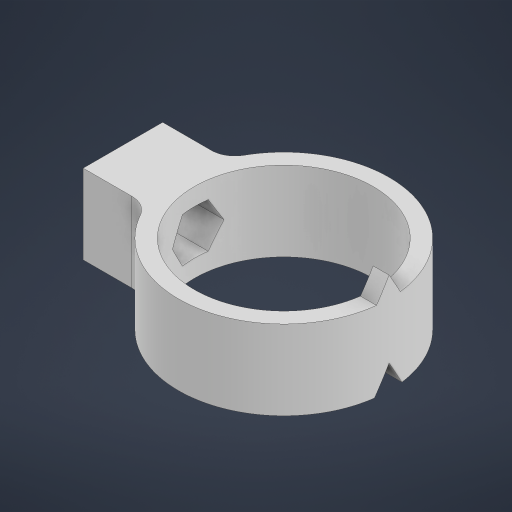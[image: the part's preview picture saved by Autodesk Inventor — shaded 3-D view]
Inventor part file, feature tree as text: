
AUTODESK INVENTOR PART (.ipt)
format: ipt  version: 2023 (Build 270158000, 158)  size: 243,712 bytes
history: native  units: mm
features: extrude x6, sketch x5, plane x2, fillet x1, projected_geometry x1
ambient origin geometry x8: Origin, YZ Plane, XZ Plane, XY Plane, X Axis, Y Axis, Z Axis, Center Point
bodies: Solid1 (feature_tree)
feature tree (15):
  extrude  "Extrusion1"  Depth=2.0mm
  plane  "Work Plane1"
  extrude  "Extrusion2"  Depth=10.0mm
  extrude  "Extrusion3"  TaperAngle=60.0deg  [1 undecoded]
  plane  "Work Plane2"
  extrude  "Extrusion4"  Depth=3.0mm TaperAngle=0.0deg
  sketch  "Sketch7"  dims[d11=60.0deg d12=12.25mm d13=0.0mm d14=-20.25mm d16=0.2mm d18=10.25mm d19=0.0mm d20=6.5mm d21=60.0mm d23=360.0deg d25=3.6mm d26=10.0mm d27=0.0mm d28=5.0mm d29=0.0mm d30=3.0mm]
  extrude  "Extrusion5"  Depth=3.0mm TaperAngle=0.0deg
  extrude  "Extrusion6"  [1 undecoded]
  fillet  "Fillet1"  Radius=0.2mm
  sketch  "Sketch1"  dims[d0=22.5mm d1=2.0mm]
  sketch  "Sketch2"  dims[d2=10.0mm d3=0.0mm d4=15.5mm]
  projected_geometry  "Projected Loop1"
  sketch  "Sketch3"  dims[d5=60.0deg d7=60.0deg]
  sketch  "Sketch5"  dims[d8=3.0mm d9=12.25mm d10=0.0mm]
note: 2 required parameter values undecoded (feature->parameter linkage not recoverable at this tier; creation-order binding heuristic only, values carry confidence <= 0.55)
